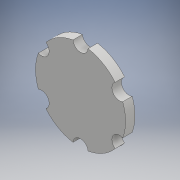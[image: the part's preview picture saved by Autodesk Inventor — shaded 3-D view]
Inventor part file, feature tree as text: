
AUTODESK INVENTOR PART (.ipt)
format: ipt  version: 2017 (Build 210142000, 142)  size: 125,952 bytes
history: native  units: mm
features: extrude x2, sketch x2
ambient origin geometry x8: Origin, YZ Plane, XZ Plane, XY Plane, X Axis, Y Axis, Z Axis, Center Point
bodies: Solid1 (feature_tree)
feature tree (4):
  extrude  "Extrusion1"  Depth=3.2mm
  extrude  "Extrusion2"  Depth=2.0mm TaperAngle=0.0deg
  sketch  "Sketch1"  dims[d0=19.0mm d1=3.2mm]
  sketch  "Sketch2"  dims[d2=60.0mm d4=360.0deg d6=2.0mm d7=0.0mm d8=4.0mm d9=4.0mm d10=2.0mm d11=0.0mm]
